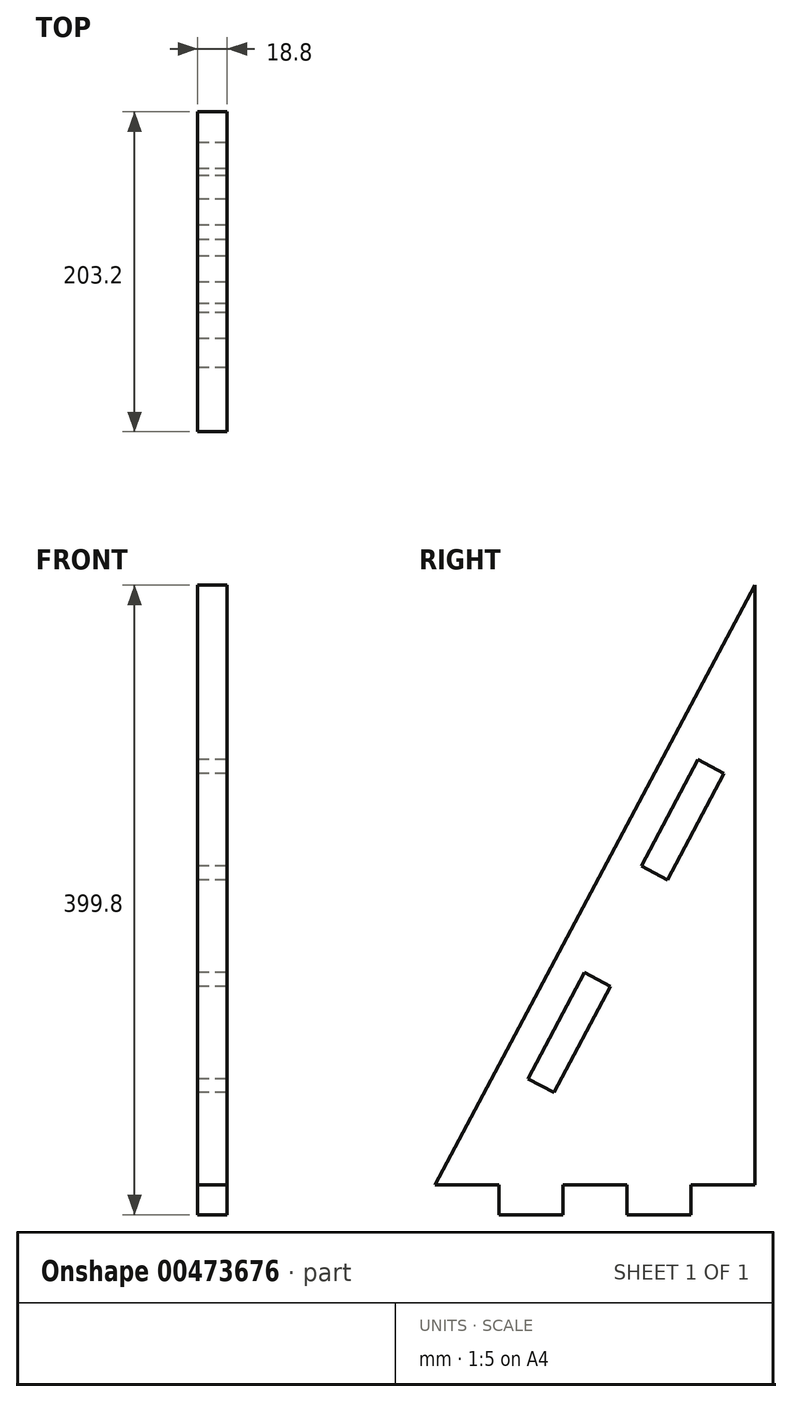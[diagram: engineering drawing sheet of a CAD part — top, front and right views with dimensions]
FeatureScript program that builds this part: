
annotation { "Feature Type Name" : "Feature", "Feature Type Description" : "" }
export const myFeature = defineFeature(function(context is Context, id is Id, definition is map)
    precondition{}
    {
        {
            var Q0;
            Q0=qCreatedBy(makeId("Right.planeOp"),FACE);
            var sketch = newSketch(context, id + "F0", { "sketchPlane" : qUnion([Q0])});
            skLineSegment(sketch, "E0", {"start": v(0, 0) * mm, "end": v(0, 381) * mm});
            skLineSegment(sketch, "E1", {"start": v(0, 381) * mm, "end": v(-203.2, 0) * mm});
            skLineSegment(sketch, "E2", {"start": v(-203.2, 0) * mm, "end": v(0, 0) * mm});
            skLineSegment(sketch, "E3.0", {"start": v(17.93, 371.44) * mm, "end": v(-185.27, -9.56) * mm});
            skPoint(sketch, "E4", {"position": v(0, 337.82) * mm});
            skPoint(sketch, "E5", {"position": v(-180.17, 0) * mm});
            skLineSegment(sketch, "E6", {"start": v(-180.17, 0) * mm, "end": v(-144.14, 67.56) * mm});
            skLineSegment(sketch, "E7", {"start": v(-144.14, 67.56) * mm, "end": v(-127.55, 58.72) * mm});
            skLineSegment(sketch, "E8", {"start": v(-127.55, 58.72) * mm, "end": v(-91.52, 126.28) * mm});
            skLineSegment(sketch, "E9", {"start": v(-91.52, 126.28) * mm, "end": v(-108.1, 135.13) * mm});
            skLineSegment(sketch, "E10", {"start": v(-108.1, 135.13) * mm, "end": v(-72.07, 202.69) * mm});
            skLineSegment(sketch, "E11", {"start": v(-72.07, 202.69) * mm, "end": v(-55.49, 193.84) * mm});
            skLineSegment(sketch, "E12", {"start": v(-55.49, 193.84) * mm, "end": v(-19.45, 261.4) * mm});
            skLineSegment(sketch, "E13", {"start": v(-19.45, 261.4) * mm, "end": v(-36.04, 270.25) * mm});
            skLineSegment(sketch, "E14", {"start": v(-36.04, 270.25) * mm, "end": v(0, 337.82) * mm});
            skLineSegment(sketch, "E15", {"start": v(-101.6, 0) * mm, "end": v(-162.56, 0) * mm});
            skLineSegment(sketch, "E16", {"start": v(-162.56, 0) * mm, "end": v(-162.56, -18.8) * mm});
            skLineSegment(sketch, "E17", {"start": v(-162.56, -18.8) * mm, "end": v(-121.92, -18.8) * mm});
            skLineSegment(sketch, "E18", {"start": v(-121.92, -18.8) * mm, "end": v(-121.92, 0) * mm});
            skLineSegment(sketch, "E19", {"start": v(-121.92, 0) * mm, "end": v(-162.56, 0) * mm});
            skLineSegment(sketch, "E20", {"start": v(-101.6, 0) * mm, "end": v(-40.64, 0) * mm});
            skLineSegment(sketch, "E21", {"start": v(-40.64, 0) * mm, "end": v(-40.64, -18.8) * mm});
            skLineSegment(sketch, "E22", {"start": v(-40.64, -18.8) * mm, "end": v(-81.28, -18.8) * mm});
            skLineSegment(sketch, "E23", {"start": v(-81.28, -18.8) * mm, "end": v(-81.28, 0) * mm});
            skLineSegment(sketch, "E24", {"start": v(-81.28, 0) * mm, "end": v(-40.64, 0) * mm});
            skSolve(sketch);
        }
        {
            var Q0;
            Q0=qSketchRegion(id+"F0",true);
            extrude(context, id + "F1", {"entities" : qUnion([Q0]), "depth" : 18.8 * mm, "offsetDistance" : 25.4 * mm});
        }
    });
